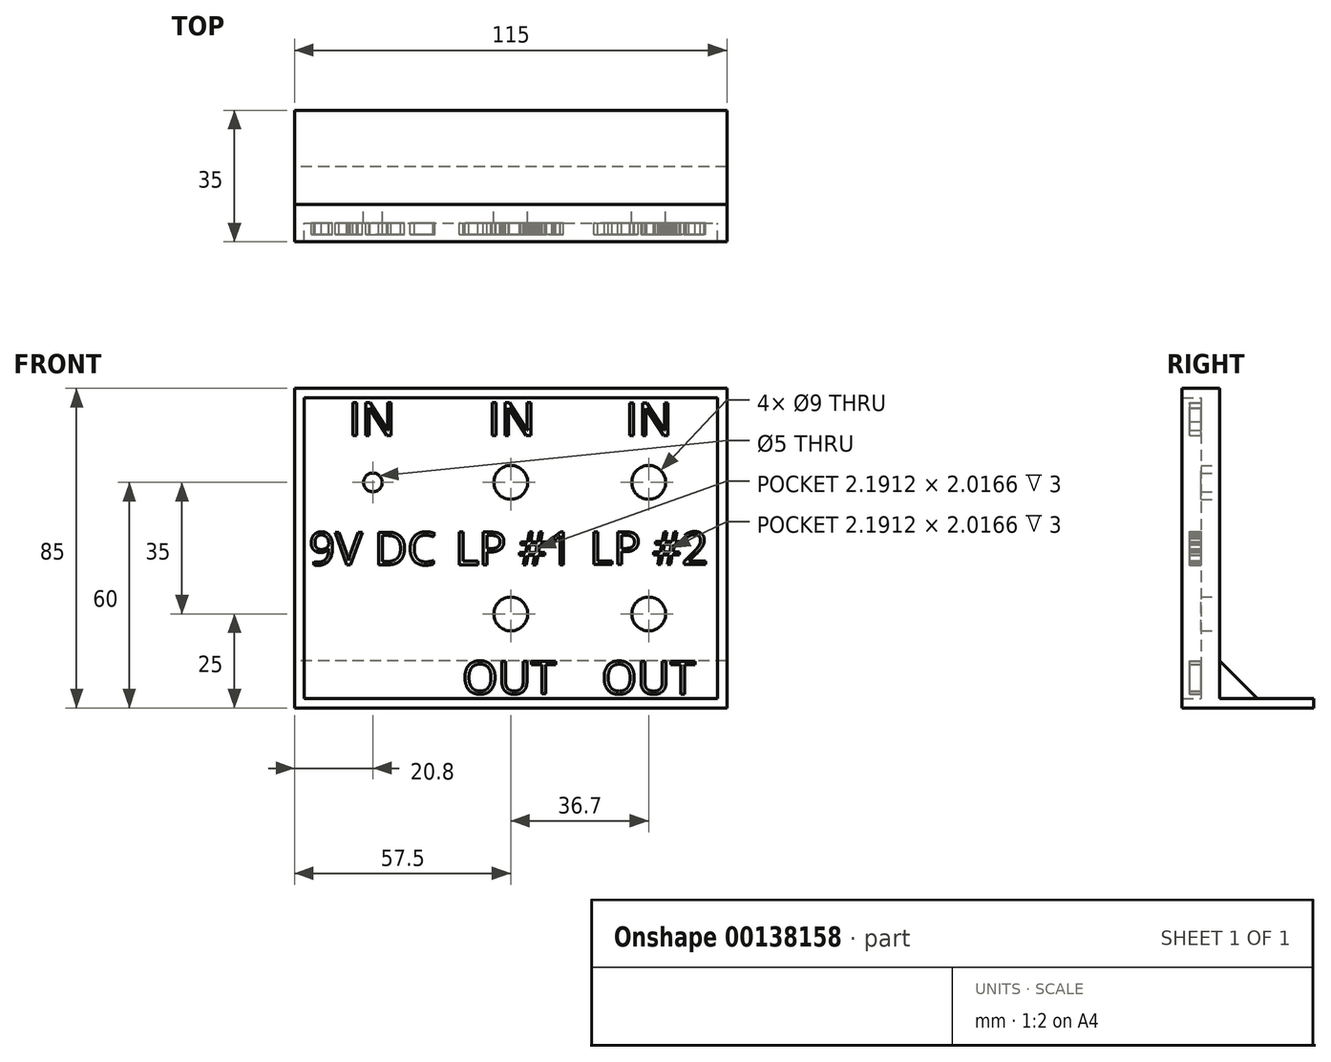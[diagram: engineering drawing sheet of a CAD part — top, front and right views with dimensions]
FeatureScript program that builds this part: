
annotation { "Feature Type Name" : "Feature", "Feature Type Description" : "" }
export const myFeature = defineFeature(function(context is Context, id is Id, definition is map)
    precondition{}
    {
        {
            var Q0;
            Q0=qCreatedBy(makeId("Front.planeOp"),FACE);
            var sketch = newSketch(context, id + "F0", { "sketchPlane" : qUnion([Q0])});
            skLineSegment(sketch, "E0.bottom", {"start": v(-55, 40) * mm, "end": v(55, 40) * mm});
            skLineSegment(sketch, "E0.top", {"start": v(-55, -40) * mm, "end": v(55, -40) * mm});
            skLineSegment(sketch, "E0.left", {"start": v(-55, 40) * mm, "end": v(-55, -40) * mm});
            skLineSegment(sketch, "E0.right", {"start": v(55, 40) * mm, "end": v(55, -40) * mm});
            skPoint(sketch, "E0.middle", {"position": v(0, 0) * mm});
            skLineSegment(sketch, "E1.bottom", {"start": v(-57.5, 42.5) * mm, "end": v(57.5, 42.5) * mm});
            skLineSegment(sketch, "E1.top", {"start": v(-57.5, -42.5) * mm, "end": v(57.5, -42.5) * mm});
            skLineSegment(sketch, "E1.left", {"start": v(-57.5, 42.5) * mm, "end": v(-57.5, -42.5) * mm});
            skLineSegment(sketch, "E1.right", {"start": v(57.5, 42.5) * mm, "end": v(57.5, -42.5) * mm});
            skPoint(sketch, "E2", {"position": v(55, 0) * mm});
            skPoint(sketch, "E3", {"position": v(-55, 0) * mm});
            skPoint(sketch, "E4", {"position": v(-55, 5) * mm});
            skPoint(sketch, "E5", {"position": v(-55, -5) * mm});
            skPoint(sketch, "E6", {"position": v(55, 5) * mm});
            skPoint(sketch, "E7", {"position": v(55, -5) * mm});
            skPoint(sketch, "E8", {"position": v(-55, -30) * mm});
            skPoint(sketch, "E9", {"position": v(-55, 30) * mm});
            skPoint(sketch, "E10", {"position": v(55, -30) * mm});
            skPoint(sketch, "E11", {"position": v(55, 30) * mm});
            skLineSegment(sketch, "E12", {"start": v(-55, 30) * mm, "end": v(55, 30) * mm, "construction": true});
            skLineSegment(sketch, "E13", {"start": v(-55, -30) * mm, "end": v(55, -30) * mm, "construction": true});
            skLineSegment(sketch, "E14", {"start": v(-55, 5) * mm, "end": v(55, 5) * mm, "construction": true});
            skLineSegment(sketch, "E15", {"start": v(-55, -5) * mm, "end": v(55, -5) * mm, "construction": true});
            skPoint(sketch, "E16", {"position": v(-18.4, 40) * mm});
            skPoint(sketch, "E17", {"position": v(18.4, 40) * mm});
            skPoint(sketch, "E18", {"position": v(-18.4, -40) * mm});
            skPoint(sketch, "E19", {"position": v(18.4, -40) * mm});
            skLineSegment(sketch, "E20", {"start": v(-18.4, 40) * mm, "end": v(-18.4, -40) * mm, "construction": true});
            skLineSegment(sketch, "E21", {"start": v(18.4, 40) * mm, "end": v(18.4, -40) * mm, "construction": true});
            skPoint(sketch, "E22", {"position": v(-18.4, 30) * mm});
            skPoint(sketch, "E23", {"position": v(-18.4, 5) * mm});
            skPoint(sketch, "E24", {"position": v(18.4, 5) * mm});
            skPoint(sketch, "E25", {"position": v(18.4, 30) * mm});
            skPoint(sketch, "E26", {"position": v(18.4, -5) * mm});
            skPoint(sketch, "E27", {"position": v(-18.4, -5) * mm});
            skPoint(sketch, "E28", {"position": v(-18.4, -30) * mm});
            skPoint(sketch, "E29", {"position": v(18.4, -30) * mm});
            skLineSegment(sketch, "E30", {"start": v(-55, 30) * mm, "end": v(-18.4, 5) * mm, "construction": true});
            skLineSegment(sketch, "E31", {"start": v(-18.4, 30) * mm, "end": v(-55, 5) * mm, "construction": true});
            skLineSegment(sketch, "E32", {"start": v(-18.4, 30) * mm, "end": v(18.4, 5) * mm, "construction": true});
            skLineSegment(sketch, "E33", {"start": v(18.4, 30) * mm, "end": v(-18.4, 5) * mm, "construction": true});
            skLineSegment(sketch, "E34", {"start": v(18.4, 30) * mm, "end": v(55, 5) * mm, "construction": true});
            skLineSegment(sketch, "E35", {"start": v(55, 30) * mm, "end": v(18.4, 5) * mm, "construction": true});
            skLineSegment(sketch, "E36", {"start": v(18.4, -5) * mm, "end": v(55, -30) * mm, "construction": true});
            skLineSegment(sketch, "E37", {"start": v(55, -5) * mm, "end": v(18.4, -30) * mm, "construction": true});
            skLineSegment(sketch, "E38", {"start": v(-18.4, -5) * mm, "end": v(18.4, -30) * mm, "construction": true});
            skLineSegment(sketch, "E39", {"start": v(18.4, -5) * mm, "end": v(-18.4, -30) * mm, "construction": true});
            skLineSegment(sketch, "E40", {"start": v(-55, -5) * mm, "end": v(-18.4, -30) * mm, "construction": true});
            skLineSegment(sketch, "E41", {"start": v(-18.4, -5) * mm, "end": v(-55, -30) * mm, "construction": true});
            skPoint(sketch, "E42", {"position": v(-36.7, 17.5) * mm});
            skPoint(sketch, "E43", {"position": v(0, 17.5) * mm});
            skPoint(sketch, "E44", {"position": v(36.7, 17.5) * mm});
            skPoint(sketch, "E45", {"position": v(36.7, -17.5) * mm});
            skPoint(sketch, "E46", {"position": v(0, -17.5) * mm});
            skPoint(sketch, "E47", {"position": v(-36.7, -17.5) * mm});
            skCircle(sketch, "E48", {"center": v(-36.7, 17.5) * mm, "radius": 2.5 * mm});
            skCircle(sketch, "E49", {"center": v(0, 17.5) * mm, "radius": 4.5 * mm});
            skCircle(sketch, "E50", {"center": v(36.7, 17.5) * mm, "radius": 4.5 * mm});
            skCircle(sketch, "E51", {"center": v(36.7, -17.5) * mm, "radius": 4.5 * mm});
            skCircle(sketch, "E52", {"center": v(0, -17.5) * mm, "radius": 4.5 * mm});
            skPoint(sketch, "E53", {"position": v(-57.5, -40) * mm});
            skPoint(sketch, "E54", {"position": v(57.5, -40) * mm});
            skLineSegment(sketch, "E55", {"start": v(-55, -40) * mm, "end": v(-57.5, -40) * mm});
            skLineSegment(sketch, "E56", {"start": v(57.5, -40) * mm, "end": v(55, -40) * mm});
            skLineSegment(sketch, "E57", {"start": v(-55, 40) * mm, "end": v(-18.4, 30) * mm, "construction": true});
            skLineSegment(sketch, "E58", {"start": v(-18.4, 40) * mm, "end": v(-55, 30) * mm, "construction": true});
            skLineSegment(sketch, "E59", {"start": v(-18.4, 40) * mm, "end": v(18.4, 30) * mm, "construction": true});
            skLineSegment(sketch, "E60", {"start": v(18.4, 40) * mm, "end": v(-18.4, 30) * mm, "construction": true});
            skLineSegment(sketch, "E61", {"start": v(18.4, 40) * mm, "end": v(55, 30) * mm, "construction": true});
            skLineSegment(sketch, "E62", {"start": v(55, 40) * mm, "end": v(18.4, 30) * mm, "construction": true});
            skLineSegment(sketch, "E63", {"start": v(55, -5) * mm, "end": v(18.4, 5) * mm, "construction": true});
            skLineSegment(sketch, "E64", {"start": v(55, 5) * mm, "end": v(18.4, -5) * mm, "construction": true});
            skLineSegment(sketch, "E65", {"start": v(-18.4, 5) * mm, "end": v(18.4, -5) * mm, "construction": true});
            skLineSegment(sketch, "E66", {"start": v(18.4, 5) * mm, "end": v(-18.4, -5) * mm, "construction": true});
            skLineSegment(sketch, "E67", {"start": v(-18.4, -5) * mm, "end": v(-55, 5) * mm, "construction": true});
            skLineSegment(sketch, "E68", {"start": v(-18.4, 5) * mm, "end": v(-55, -5) * mm, "construction": true});
            skLineSegment(sketch, "E69", {"start": v(-55, -30) * mm, "end": v(-18.4, -40) * mm, "construction": true});
            skLineSegment(sketch, "E70", {"start": v(-18.4, -30) * mm, "end": v(-55, -40) * mm, "construction": true});
            skLineSegment(sketch, "E71", {"start": v(-18.4, -30) * mm, "end": v(18.4, -40) * mm, "construction": true});
            skLineSegment(sketch, "E72", {"start": v(18.4, -30) * mm, "end": v(-18.4, -40) * mm, "construction": true});
            skLineSegment(sketch, "E73", {"start": v(18.4, -30) * mm, "end": v(55, -40) * mm, "construction": true});
            skLineSegment(sketch, "E74", {"start": v(55, -30) * mm, "end": v(18.4, -40) * mm, "construction": true});
            skText(sketch, "E75", { "text": "IN", "fontName": "OpenSans-Regular.ttf"});
            skText(sketch, "E76", { "text": "IN", "fontName": "OpenSans-Regular.ttf"});
            skPoint(sketch, "E77", {"position": v(0, 40) * mm});
            skText(sketch, "E78", { "text": "IN", "fontName": "OpenSans-Regular.ttf"});
            skText(sketch, "E79", { "text": "9V DC", "fontName": "OpenSans-Regular.ttf"});
            skText(sketch, "E80", { "text": "OUT", "fontName": "OpenSans-Regular.ttf"});
            skText(sketch, "E81", { "text": "OUT", "fontName": "OpenSans-Regular.ttf"});
            skText(sketch, "E82", { "text": "LP #2", "fontName": "OpenSans-Regular.ttf"});
            skText(sketch, "E83", { "text": "LP #1", "fontName": "OpenSans-Regular.ttf"});
            const initialGuessF0  = {"E75": [0.0305, 0.02993, 1, 0, 0.00875], "E76": [-0.00607, 0.03, 1, 0, 0.00875], "E78": [-0.04317, 0.03, 1, 0, 0.00875], "E79": [-0.05372, -0.00443, 1, 0, 0.00875], "E80": [0.0241, -0.0388, 1, 0, 0.00875], "E81": [-0.01293, -0.03876, 1, 0, 0.00875], "E82": [0.02093, -0.00436, 1, 0, 0.00875], "E83": [-0.01484, -0.0044, 1, 0, 0.00875]};
            skSetInitialGuess(sketch, initialGuessF0);
            skSolve(sketch);
        }
        {
            var Q0;
            Q0=makeQuery(id+"F0.imprint","IMPRINT",FACE,{"disambiguationData":[TD([[makeQuery(id+"F0.imprint","IMPRINT",EDGE,{"derivedFrom":sQuery(id+"F0.wireOp",EDGE,"E0.bottom")}),-1.0]])]});
            var Q1;
            Q1=makeQuery(id+"F0.imprint","IMPRINT",FACE,{"disambiguationData":[TD([[makeQuery(id+"F0.imprint","IMPRINT",EDGE,{"derivedFrom":sQuery(id+"F0.wireOp",EDGE,"E79.sketch_text.stroke-16")}),1.0]])]});
            var Q2;
            Q2=makeQuery(id+"F0.imprint","IMPRINT",FACE,{"disambiguationData":[TD([[makeQuery(id+"F0.imprint","IMPRINT",EDGE,{"derivedFrom":sQuery(id+"F0.wireOp",EDGE,"E79.sketch_text.stroke-42")}),1.0]])]});
            var Q3;
            Q3=makeQuery(id+"F0.imprint","IMPRINT",FACE,{"disambiguationData":[TD([[makeQuery(id+"F0.imprint","IMPRINT",EDGE,{"derivedFrom":sQuery(id+"F0.wireOp",EDGE,"E81.sketch_text.stroke-8")}),1.0]])]});
            var Q4;
            Q4=makeQuery(id+"F0.imprint","IMPRINT",FACE,{"disambiguationData":[TD([[makeQuery(id+"F0.imprint","IMPRINT",EDGE,{"derivedFrom":sQuery(id+"F0.wireOp",EDGE,"E80.sketch_text.stroke-8")}),1.0]])]});
            var Q5;
            Q5=makeQuery(id+"F0.imprint","IMPRINT",FACE,{"disambiguationData":[TD([[makeQuery(id+"F0.imprint","IMPRINT",EDGE,{"derivedFrom":sQuery(id+"F0.wireOp",EDGE,"E82.sketch_text.stroke-49")}),1.0]])]});
            var Q6;
            Q6=makeQuery(id+"F0.imprint","IMPRINT",FACE,{"disambiguationData":[TD([[makeQuery(id+"F0.imprint","IMPRINT",EDGE,{"derivedFrom":sQuery(id+"F0.wireOp",EDGE,"E82.sketch_text.stroke-14")}),1.0]])]});
            var Q7;
            Q7=makeQuery(id+"F0.imprint","IMPRINT",FACE,{"disambiguationData":[TD([[makeQuery(id+"F0.imprint","IMPRINT",EDGE,{"derivedFrom":sQuery(id+"F0.wireOp",EDGE,"E83.sketch_text.stroke-49")}),1.0]])]});
            var Q8;
            Q8=makeQuery(id+"F0.imprint","IMPRINT",FACE,{"disambiguationData":[TD([[makeQuery(id+"F0.imprint","IMPRINT",EDGE,{"derivedFrom":sQuery(id+"F0.wireOp",EDGE,"E83.sketch_text.stroke-14")}),1.0]])]});
            extrude(context, id + "F1", {"entities" : qUnion([Q0, Q1, Q2, Q3, Q4, Q5, Q6, Q7, Q8]), "depth" : 5 * mm});
        }
        {
            var Q0;
            Q0=makeQuery(id+"F0.imprint","IMPRINT",FACE,{"disambiguationData":[TD([[makeQuery(id+"F0.imprint","IMPRINT",EDGE,{"derivedFrom":sQuery(id+"F0.wireOp",EDGE,"E0.bottom")}),1.0]])]});
            extrude(context, id + "F2", {"entities" : qUnion([Q0]), "operationType" : NewBodyOperationType.ADD, "depth" : 10 * mm});
        }
        {
            var Q0;
            Q0=makeQuery(id+"F0.imprint","IMPRINT",FACE,{"disambiguationData":[TD([[makeQuery(id+"F0.imprint","IMPRINT",EDGE,{"derivedFrom":sQuery(id+"F0.wireOp",EDGE,"E0.top")}),-1.0]])]});
            extrude(context, id + "F3", {"entities" : qUnion([Q0]), "operationType" : NewBodyOperationType.ADD, "depth" : 10 * mm, "hasSecondDirection" : true, "secondDirectionOppositeDirection" : true, "secondDirectionDepth" : 25 * mm});
        }
        {
            var Q0;
            Q0=makeQuery(id+"F0.imprint","IMPRINT",FACE,{"disambiguationData":[TD([[makeQuery(id+"F0.imprint","IMPRINT",EDGE,{"derivedFrom":sQuery(id+"F0.wireOp",EDGE,"E75.sketch_text.stroke-4")}),-1.0]])]});
            var Q1;
            Q1=makeQuery(id+"F0.imprint","IMPRINT",FACE,{"disambiguationData":[TD([[makeQuery(id+"F0.imprint","IMPRINT",EDGE,{"derivedFrom":sQuery(id+"F0.wireOp",EDGE,"E75.sketch_text.stroke-0")}),-1.0]])]});
            var Q2;
            Q2=makeQuery(id+"F0.imprint","IMPRINT",FACE,{"disambiguationData":[TD([[makeQuery(id+"F0.imprint","IMPRINT",EDGE,{"derivedFrom":sQuery(id+"F0.wireOp",EDGE,"E76.sketch_text.stroke-0")}),-1.0]])]});
            var Q3;
            Q3=makeQuery(id+"F0.imprint","IMPRINT",FACE,{"disambiguationData":[TD([[makeQuery(id+"F0.imprint","IMPRINT",EDGE,{"derivedFrom":sQuery(id+"F0.wireOp",EDGE,"E76.sketch_text.stroke-4")}),-1.0]])]});
            var Q4;
            Q4=makeQuery(id+"F0.imprint","IMPRINT",FACE,{"disambiguationData":[TD([[makeQuery(id+"F0.imprint","IMPRINT",EDGE,{"derivedFrom":sQuery(id+"F0.wireOp",EDGE,"E78.sketch_text.stroke-0")}),-1.0]])]});
            var Q5;
            Q5=makeQuery(id+"F0.imprint","IMPRINT",FACE,{"disambiguationData":[TD([[makeQuery(id+"F0.imprint","IMPRINT",EDGE,{"derivedFrom":sQuery(id+"F0.wireOp",EDGE,"E78.sketch_text.stroke-4")}),-1.0]])]});
            var Q6;
            Q6=makeQuery(id+"F0.imprint","IMPRINT",FACE,{"disambiguationData":[TD([[makeQuery(id+"F0.imprint","IMPRINT",EDGE,{"derivedFrom":sQuery(id+"F0.wireOp",EDGE,"E79.sketch_text.stroke-26")}),-1.0]])]});
            var Q7;
            Q7=makeQuery(id+"F0.imprint","IMPRINT",FACE,{"disambiguationData":[TD([[makeQuery(id+"F0.imprint","IMPRINT",EDGE,{"derivedFrom":sQuery(id+"F0.wireOp",EDGE,"E79.sketch_text.stroke-0")}),-1.0]])]});
            var Q8;
            Q8=makeQuery(id+"F0.imprint","IMPRINT",FACE,{"disambiguationData":[TD([[makeQuery(id+"F0.imprint","IMPRINT",EDGE,{"derivedFrom":sQuery(id+"F0.wireOp",EDGE,"E79.sketch_text.stroke-35")}),-1.0]])]});
            var Q9;
            Q9=makeQuery(id+"F0.imprint","IMPRINT",FACE,{"disambiguationData":[TD([[makeQuery(id+"F0.imprint","IMPRINT",EDGE,{"derivedFrom":sQuery(id+"F0.wireOp",EDGE,"E79.sketch_text.stroke-49")}),-1.0]])]});
            var Q10;
            Q10=makeQuery(id+"F0.imprint","IMPRINT",FACE,{"disambiguationData":[TD([[makeQuery(id+"F0.imprint","IMPRINT",EDGE,{"derivedFrom":sQuery(id+"F0.wireOp",EDGE,"E83.sketch_text.stroke-0")}),-1.0]])]});
            var Q11;
            Q11=makeQuery(id+"F0.imprint","IMPRINT",FACE,{"disambiguationData":[TD([[makeQuery(id+"F0.imprint","IMPRINT",EDGE,{"derivedFrom":sQuery(id+"F0.wireOp",EDGE,"E83.sketch_text.stroke-6")}),-1.0]])]});
            var Q12;
            Q12=makeQuery(id+"F0.imprint","IMPRINT",FACE,{"disambiguationData":[TD([[makeQuery(id+"F0.imprint","IMPRINT",EDGE,{"derivedFrom":sQuery(id+"F0.wireOp",EDGE,"E83.sketch_text.stroke-21")}),-1.0]])]});
            var Q13;
            Q13=makeQuery(id+"F0.imprint","IMPRINT",FACE,{"disambiguationData":[TD([[makeQuery(id+"F0.imprint","IMPRINT",EDGE,{"derivedFrom":sQuery(id+"F0.wireOp",EDGE,"E83.sketch_text.stroke-53")}),-1.0]])]});
            var Q14;
            Q14=makeQuery(id+"F0.imprint","IMPRINT",FACE,{"disambiguationData":[TD([[makeQuery(id+"F0.imprint","IMPRINT",EDGE,{"derivedFrom":sQuery(id+"F0.wireOp",EDGE,"E82.sketch_text.stroke-0")}),-1.0]])]});
            var Q15;
            Q15=makeQuery(id+"F0.imprint","IMPRINT",FACE,{"disambiguationData":[TD([[makeQuery(id+"F0.imprint","IMPRINT",EDGE,{"derivedFrom":sQuery(id+"F0.wireOp",EDGE,"E82.sketch_text.stroke-6")}),-1.0]])]});
            var Q16;
            Q16=makeQuery(id+"F0.imprint","IMPRINT",FACE,{"disambiguationData":[TD([[makeQuery(id+"F0.imprint","IMPRINT",EDGE,{"derivedFrom":sQuery(id+"F0.wireOp",EDGE,"E82.sketch_text.stroke-21")}),-1.0]])]});
            var Q17;
            Q17=makeQuery(id+"F0.imprint","IMPRINT",FACE,{"disambiguationData":[TD([[makeQuery(id+"F0.imprint","IMPRINT",EDGE,{"derivedFrom":sQuery(id+"F0.wireOp",EDGE,"E82.sketch_text.stroke-53")}),-1.0]])]});
            var Q18;
            Q18=makeQuery(id+"F0.imprint","IMPRINT",FACE,{"disambiguationData":[TD([[makeQuery(id+"F0.imprint","IMPRINT",EDGE,{"derivedFrom":sQuery(id+"F0.wireOp",EDGE,"E80.sketch_text.stroke-30")}),-1.0]])]});
            var Q19;
            Q19=makeQuery(id+"F0.imprint","IMPRINT",FACE,{"disambiguationData":[TD([[makeQuery(id+"F0.imprint","IMPRINT",EDGE,{"derivedFrom":sQuery(id+"F0.wireOp",EDGE,"E80.sketch_text.stroke-16")}),-1.0]])]});
            var Q20;
            Q20=makeQuery(id+"F0.imprint","IMPRINT",FACE,{"disambiguationData":[TD([[makeQuery(id+"F0.imprint","IMPRINT",EDGE,{"derivedFrom":sQuery(id+"F0.wireOp",EDGE,"E80.sketch_text.stroke-0")}),-1.0]])]});
            var Q21;
            Q21=makeQuery(id+"F0.imprint","IMPRINT",FACE,{"disambiguationData":[TD([[makeQuery(id+"F0.imprint","IMPRINT",EDGE,{"derivedFrom":sQuery(id+"F0.wireOp",EDGE,"E81.sketch_text.stroke-30")}),-1.0]])]});
            var Q22;
            Q22=makeQuery(id+"F0.imprint","IMPRINT",FACE,{"disambiguationData":[TD([[makeQuery(id+"F0.imprint","IMPRINT",EDGE,{"derivedFrom":sQuery(id+"F0.wireOp",EDGE,"E81.sketch_text.stroke-16")}),-1.0]])]});
            var Q23;
            Q23=makeQuery(id+"F0.imprint","IMPRINT",FACE,{"disambiguationData":[TD([[makeQuery(id+"F0.imprint","IMPRINT",EDGE,{"derivedFrom":sQuery(id+"F0.wireOp",EDGE,"E81.sketch_text.stroke-0")}),-1.0]])]});
            extrude(context, id + "F4", {"entities" : qUnion([Q0, Q1, Q2, Q3, Q4, Q5, Q6, Q7, Q8, Q9, Q10, Q11, Q12, Q13, Q14, Q15, Q16, Q17, Q18, Q19, Q20, Q21, Q22, Q23]), "operationType" : NewBodyOperationType.ADD, "depth" : 8 * mm});
        }
        {
            var Q0;
            Q0=qCreatedBy(makeId("Right.planeOp"),FACE);
            var sketch = newSketch(context, id + "F5", { "sketchPlane" : qUnion([Q0])});
            skLineSegment(sketch, "E84", {"start": v(0, -40) * mm, "end": v(0, -30) * mm});
            skLineSegment(sketch, "E85", {"start": v(0, -30) * mm, "end": v(10, -40) * mm});
            skLineSegment(sketch, "E86", {"start": v(10, -40) * mm, "end": v(0, -40) * mm});
            skSolve(sketch);
        }
        {
            var Q0;
            Q0=makeQuery(id+"F5.imprint","IMPRINT",FACE,{"disambiguationData":[TD([[makeQuery(id+"F5.imprint","IMPRINT",EDGE,{"derivedFrom":sQuery(id+"F5.wireOp",EDGE,"E84")}),-1.0]])]});
            extrude(context, id + "F6", {"entities" : qUnion([Q0]), "depth" : 115 * mm, "symmetric" : true});
        }
    });
